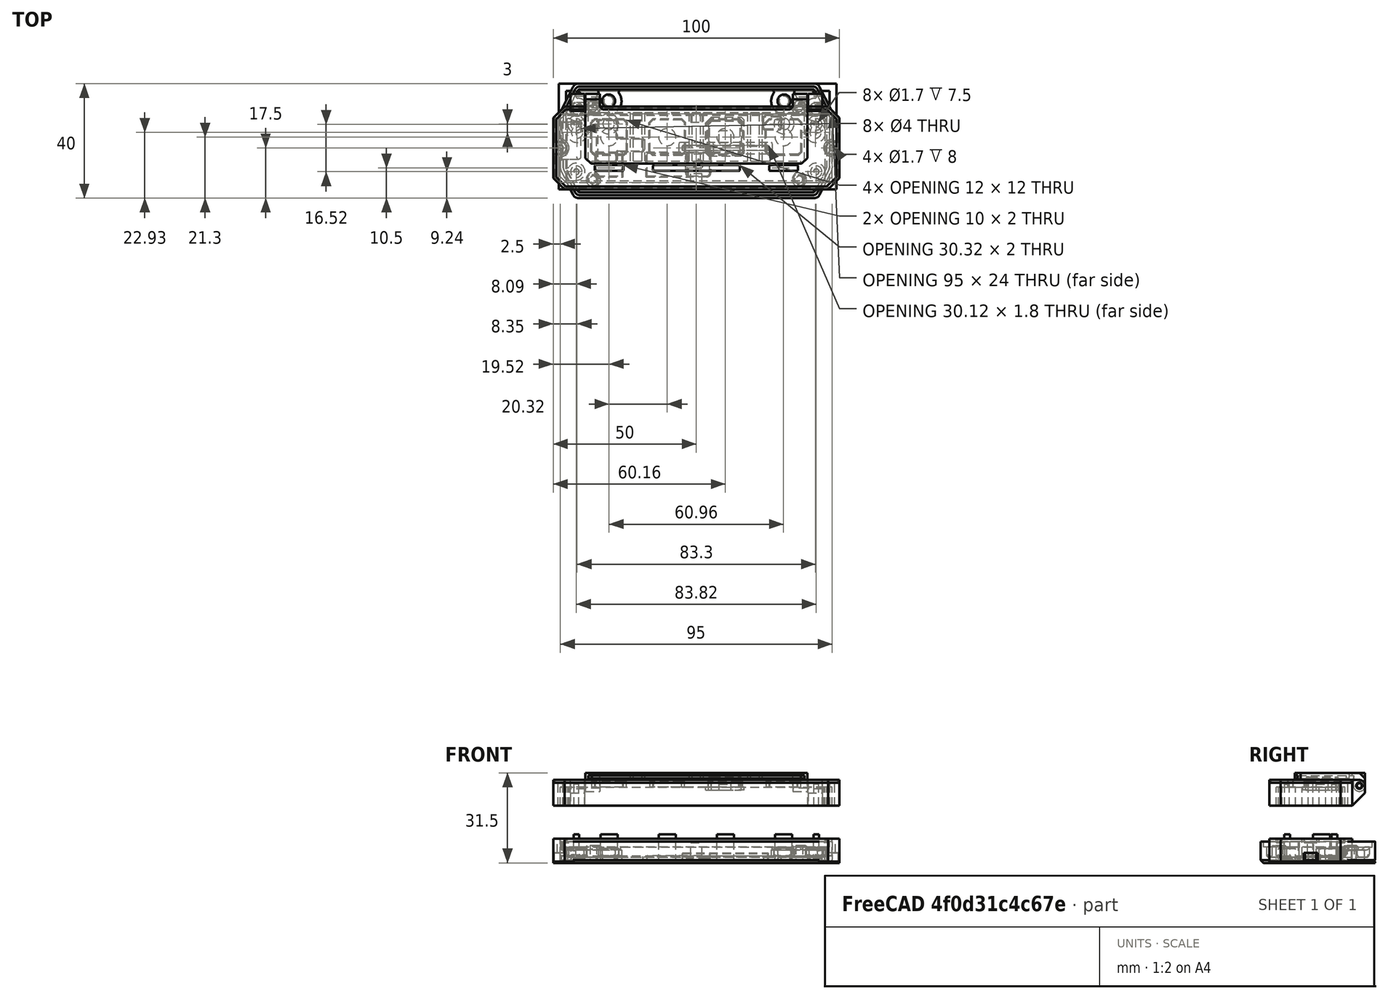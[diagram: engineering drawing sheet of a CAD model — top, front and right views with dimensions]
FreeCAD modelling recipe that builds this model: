
FCSTD DOCUMENT  (FreeCAD 0.18R16146 (Git))
Label: klipper-button
License: All rights reserved
LicenseURL: http://en.wikipedia.org/wiki/All_rights_reserved
objects: Part::Cylinder×46, Part::Box×43, Part::MultiFuse×27, Part::Cut×23, Part::Chamfer×19, Part::Feature×11, Part::Fillet×4
note: 173 computed .brp shape members not serialized (recipe doc carries the construction recipe); baked Part::Feature solids carry a one-line shape summary decoded from their .brp

FEATURE [Part::Feature] Part__Feature001001  label="Housing002"
  Placement = pos=(-10,2.5,0) rot=(0,0,1;0rad)
  shape: bbox 95.02 x 40.02 x 7.633 mm, 303 faces (baked)
FEATURE [Part::Cylinder] Cylinder
  Angle = 360
  AttacherType = Attacher::AttachEngine3D
  Height = 10
  Placement = pos=(-25.65,13.93,0) rot=(0,0,1;0rad)
  Radius = 2
FEATURE [Part::Cylinder] Cylinder001
  Angle = 360
  AttacherType = Attacher::AttachEngine3D
  Height = 10
  Placement = pos=(-36.65,10.93,0) rot=(0,0,1;0rad)
  Radius = 2
FEATURE [Part::Cylinder] Cylinder002
  Angle = 360
  AttacherType = Attacher::AttachEngine3D
  Height = 10
  Placement = pos=(46.65,10.93,0) rot=(0,0,1;0rad)
  Radius = 2
FEATURE [Part::Cylinder] Cylinder003
  Angle = 360
  AttacherType = Attacher::AttachEngine3D
  Height = 10
  Placement = pos=(35.65,13.93,0) rot=(0,0,1;0rad)
  Radius = 2
FEATURE [Part::Box] Box  label="PCB"
  AttacherType = Attacher::AttachEngine3D
  Height = 1
  Length = 90.17
  Placement = pos=(-45.085,-11.43,7.5) rot=(0,0,1;0rad)
  Width = 22.86
FEATURE [Part::Cylinder] Cylinder004
  Angle = 360
  AttacherType = Attacher::AttachEngine3D
  Height = 7.5
  Placement = pos=(-41.91,8.255,0) rot=(0,0,1;0rad)
  Radius = 0.85
FEATURE [Part::Cylinder] Cylinder005
  Angle = 360
  AttacherType = Attacher::AttachEngine3D
  Height = 7.5
  Placement = pos=(-41.91,-8.26,0) rot=(0,0,1;0rad)
  Radius = 0.85
FEATURE [Part::Cylinder] Cylinder006
  Angle = 360
  AttacherType = Attacher::AttachEngine3D
  Height = 7.5
  Placement = pos=(41.91,8.26,0) rot=(0,0,1;0rad)
  Radius = 0.85
FEATURE [Part::Cylinder] Cylinder007
  Angle = 360
  AttacherType = Attacher::AttachEngine3D
  Height = 7.5
  Placement = pos=(41.91,-8.26,0) rot=(0,0,1;0rad)
  Radius = 0.85
FEATURE [Part::Cylinder] Cylinder008
  Angle = 360
  AttacherType = Attacher::AttachEngine3D
  Height = 10
  Placement = pos=(-10.16,3.81,0) rot=(0,0,1;0rad)
  Radius = 3
FEATURE [Part::Cylinder] Cylinder009
  Angle = 360
  AttacherType = Attacher::AttachEngine3D
  Height = 10
  Placement = pos=(10.16,3.81,0) rot=(0,0,1;0rad)
  Radius = 3
FEATURE [Part::Cylinder] Cylinder010
  Angle = 360
  AttacherType = Attacher::AttachEngine3D
  Height = 10
  Placement = pos=(30.48,3.81,0) rot=(0,0,1;0rad)
  Radius = 3
FEATURE [Part::Cylinder] Cylinder011
  Angle = 360
  AttacherType = Attacher::AttachEngine3D
  Height = 10
  Placement = pos=(-30.48,3.81,0) rot=(0,0,1;0rad)
  Radius = 3
FEATURE [Part::MultiFuse] Fusion002  label="button"
  Shapes = -> [Cylinder011,Cylinder010,Cylinder009,Cylinder008]
FEATURE [Part::Box] Box001  label="Cube001"
  AttacherType = Attacher::AttachEngine3D
  Height = 0.5
  Length = 97
  Placement = pos=(-48,-14.5,0) rot=(0,0,1;0rad)
  Width = 37
FEATURE [Part::Box] Box002  label="Cube002"
  AttacherType = Attacher::AttachEngine3D
  Height = 0.5
  Length = 92
  Placement = pos=(-45.5,-12,0) rot=(0,0,1;0rad)
  Width = 32
FEATURE [Part::Box] Box003  label="Cube003"
  AttacherType = Attacher::AttachEngine3D
  Height = 22.5
  Length = 95
  Placement = pos=(-47.5,-12,2.5) rot=(0,0,1;0rad)
  Width = 24
FEATURE [Part::Box] Box004  label="Cube004"
  AttacherType = Attacher::AttachEngine3D
  Height = 8.5
  Length = 100
  Placement = pos=(-50,-14.5,0) rot=(0,0,1;0rad)
  Width = 29
FEATURE [Part::Cylinder] Cylinder012
  Angle = 360
  AttacherType = Attacher::AttachEngine3D
  Height = 5
  Placement = pos=(46.65,10.93,0) rot=(0,0,1;0rad)
  Radius = 3.5
FEATURE [Part::Cylinder] Cylinder013
  Angle = 360
  AttacherType = Attacher::AttachEngine3D
  Height = 5
  Placement = pos=(-25.65,13.93,0) rot=(0,0,1;0rad)
  Radius = 3.5
FEATURE [Part::Cylinder] Cylinder014
  Angle = 360
  AttacherType = Attacher::AttachEngine3D
  Height = 5
  Placement = pos=(-36.65,10.93,0) rot=(0,0,1;0rad)
  Radius = 3.5
FEATURE [Part::Cylinder] Cylinder015
  Angle = 360
  AttacherType = Attacher::AttachEngine3D
  Height = 5
  Placement = pos=(35.65,13.93,0) rot=(0,0,1;0rad)
  Radius = 3.5
FEATURE [Part::MultiFuse] Fusion
  Placement = pos=(-5,-5.5,0) rot=(0,0,1;0rad)
  Shapes = -> [Cylinder002,Cylinder,Cylinder001,Cylinder003]
FEATURE [Part::MultiFuse] Fusion003
  Placement = pos=(-5,-5.5,0) rot=(0,0,1;0rad)
  Shapes = -> [Cylinder015,Cylinder014,Cylinder013,Cylinder012]
FEATURE [Part::Cylinder] Cylinder016
  Angle = 360
  AttacherType = Attacher::AttachEngine3D
  Height = 5
  Placement = pos=(-41.91,8.255,0) rot=(0,0,1;0rad)
  Radius = 3
FEATURE [Part::Cylinder] Cylinder017
  Angle = 360
  AttacherType = Attacher::AttachEngine3D
  Height = 5
  Placement = pos=(-41.91,-8.26,0) rot=(0,0,1;0rad)
  Radius = 3
FEATURE [Part::Cylinder] Cylinder018
  Angle = 360
  AttacherType = Attacher::AttachEngine3D
  Height = 5
  Placement = pos=(41.91,8.26,0) rot=(0,0,1;0rad)
  Radius = 3
FEATURE [Part::Cylinder] Cylinder019
  Angle = 360
  AttacherType = Attacher::AttachEngine3D
  Height = 5
  Placement = pos=(41.91,-8.26,0) rot=(0,0,1;0rad)
  Radius = 3
FEATURE [Part::MultiFuse] Fusion006
  Shapes = -> [Cylinder019,Cylinder016,Cylinder017,Cylinder018]
FEATURE [Part::Cylinder] Cylinder020
  Angle = 360
  AttacherType = Attacher::AttachEngine3D
  Height = 10
  Placement = pos=(41.91,-8.26,0) rot=(0,0,1;0rad)
  Radius = 1
FEATURE [Part::Cylinder] Cylinder021
  Angle = 360
  AttacherType = Attacher::AttachEngine3D
  Height = 10
  Placement = pos=(41.91,8.26,0) rot=(0,0,1;0rad)
  Radius = 1
FEATURE [Part::Cylinder] Cylinder022
  Angle = 360
  AttacherType = Attacher::AttachEngine3D
  Height = 10
  Placement = pos=(-41.91,-8.26,0) rot=(0,0,1;0rad)
  Radius = 1
FEATURE [Part::Cylinder] Cylinder023
  Angle = 360
  AttacherType = Attacher::AttachEngine3D
  Height = 10
  Placement = pos=(-41.91,8.255,0) rot=(0,0,1;0rad)
  Radius = 1
FEATURE [Part::MultiFuse] Fusion008
  Shapes = -> [Cylinder020,Cylinder021,Cylinder023,Cylinder022]
FEATURE [Part::Box] Box005  label="Cube"
  AttacherType = Attacher::AttachEngine3D
  Height = 10
  Length = 9
  Placement = pos=(-34.974,-10.755,0) rot=(0,0,1;0rad)
  Width = 8
FEATURE [Part::Box] Box006  label="Cube005"
  AttacherType = Attacher::AttachEngine3D
  Height = 10
  Length = 14
  Placement = pos=(-17.154,-10.755,0) rot=(0,0,1;0rad)
  Width = 8
FEATURE [Part::Cylinder] Cylinder024
  Angle = 360
  AttacherType = Attacher::AttachEngine3D
  Height = 1.5
  Placement = pos=(41.91,-8.26,0) rot=(0,0,1;0rad)
  Radius = 2
FEATURE [Part::Cylinder] Cylinder025
  Angle = 360
  AttacherType = Attacher::AttachEngine3D
  Height = 1.5
  Placement = pos=(-41.91,8.255,0) rot=(0,0,1;0rad)
  Radius = 2
FEATURE [Part::Cylinder] Cylinder026
  Angle = 360
  AttacherType = Attacher::AttachEngine3D
  Height = 1.5
  Placement = pos=(-41.91,-8.26,0) rot=(0,0,1;0rad)
  Radius = 2
FEATURE [Part::Cylinder] Cylinder027
  Angle = 360
  AttacherType = Attacher::AttachEngine3D
  Height = 1.5
  Placement = pos=(41.91,8.26,0) rot=(0,0,1;0rad)
  Radius = 2
FEATURE [Part::MultiFuse] Fusion012
  Shapes = -> [Cylinder027,Cylinder026,Cylinder025,Cylinder024]
FEATURE [Part::Box] Box008  label="Cube007"
  AttacherType = Attacher::AttachEngine3D
  Height = 6.5
  Length = 95
  Placement = pos=(-47.5,-12,20) rot=(0,0,1;0rad)
  Width = 24
FEATURE [Part::Cylinder] Cylinder028
  Angle = 360
  AttacherType = Attacher::AttachEngine3D
  Height = 8
  Placement = pos=(41.91,-8.26,0) rot=(0,0,1;0rad)
  Radius = 3
FEATURE [Part::Cylinder] Cylinder029
  Angle = 360
  AttacherType = Attacher::AttachEngine3D
  Height = 8
  Placement = pos=(-41.91,8.255,0) rot=(0,0,1;0rad)
  Radius = 3
FEATURE [Part::Cylinder] Cylinder030
  Angle = 360
  AttacherType = Attacher::AttachEngine3D
  Height = 8
  Placement = pos=(41.91,8.26,0) rot=(0,0,1;0rad)
  Radius = 3
FEATURE [Part::Cylinder] Cylinder031
  Angle = 360
  AttacherType = Attacher::AttachEngine3D
  Height = 8
  Placement = pos=(-41.91,-8.26,0) rot=(0,0,1;0rad)
  Radius = 3
FEATURE [Part::MultiFuse] Fusion013
  Placement = pos=(0,0,20) rot=(0,0,1;0rad)
  Shapes = -> [Cylinder031,Cylinder030,Cylinder029,Cylinder028]
FEATURE [Part::MultiFuse] Fusion015
  Placement = pos=(0,0,20) rot=(0,0,1;0rad)
  Shapes = -> [Cylinder006,Cylinder005,Cylinder004,Cylinder007]
FEATURE [Part::Box] Box009  label="Cube008"
  AttacherType = Attacher::AttachEngine3D
  Height = 10
  Length = 12
  Placement = pos=(-16.16,-6,0) rot=(0,0,1;0rad)
  Width = 12
FEATURE [Part::Box] Box010  label="Cube009"
  AttacherType = Attacher::AttachEngine3D
  Height = 10
  Length = 12
  Placement = pos=(4.16,-6,0) rot=(0,0,1;0rad)
  Width = 12
FEATURE [Part::Box] Box011  label="Cube010"
  AttacherType = Attacher::AttachEngine3D
  Height = 10
  Length = 12
  Placement = pos=(24.48,-6,0) rot=(0,0,1;0rad)
  Width = 12
FEATURE [Part::Box] Box012  label="Cube011"
  AttacherType = Attacher::AttachEngine3D
  Height = 10
  Length = 12
  Placement = pos=(-36.48,-6,0) rot=(0,0,1;0rad)
  Width = 12
FEATURE [Part::MultiFuse] Fusion016
  Placement = pos=(0,0,25) rot=(0,0,1;0rad)
  Shapes = -> [Box012,Box011,Box010,Box009]
FEATURE [Part::Chamfer] Chamfer007
  Base = -> Fusion016
  Edges = 16 edges r=1: [Edge1,Edge3,Edge5,Edge7,Edge13,Edge15,Edge17,Edge19,Edge25,Edge27,Edge29,Edge31,Edge37,Edge39,Edge41,Edge43]
  Placement = pos=(0,3.8,0) rot=(0,0,1;0rad)
FEATURE [Part::Cut] Cut
  Base = -> Box004
  Tool = -> Box003
FEATURE [Part::MultiFuse] Fusion017
  Shapes = -> [Cut,Fusion003]
FEATURE [Part::Cut] Cut008
  Base = -> Fusion017
  Tool = -> Fusion
FEATURE [Part::Box] Box007  label="Cube006"
  AttacherType = Attacher::AttachEngine3D
  Height = 9
  Length = 100
  Placement = pos=(-50,-14.5,20) rot=(0,0,1;0rad)
  Width = 29
FEATURE [Part::Cut] Cut010
  Base = -> Box007
  Tool = -> Box008
FEATURE [Part::MultiFuse] Fusion018
  Shapes = -> [Fusion013,Cut010]
FEATURE [Part::Cut] Cut011
  Base = -> Fusion018
  Tool = -> Fusion015
FEATURE [Part::Cylinder] Cylinder032
  Angle = 360
  AttacherType = Attacher::AttachEngine3D
  Height = 8
  Placement = pos=(-47.5,0,20) rot=(0,0,1;0rad)
  Radius = 3
FEATURE [Part::Cylinder] Cylinder033
  Angle = 360
  AttacherType = Attacher::AttachEngine3D
  Height = 8
  Placement = pos=(47.5,0,20) rot=(0,0,1;0rad)
  Radius = 3
FEATURE [Part::Cylinder] Cylinder034
  Angle = 360
  AttacherType = Attacher::AttachEngine3D
  Height = 3.5
  Placement = pos=(47.5,0,0) rot=(0,0,1;0rad)
  Radius = 2
FEATURE [Part::Cylinder] Cylinder035
  Angle = 360
  AttacherType = Attacher::AttachEngine3D
  Height = 3.5
  Placement = pos=(-47.5,0,0) rot=(0,0,1;0rad)
  Radius = 2
FEATURE [Part::Cylinder] Cylinder036
  Angle = 360
  AttacherType = Attacher::AttachEngine3D
  Height = 8.5
  Placement = pos=(-47.5,0,0) rot=(0,0,1;0rad)
  Radius = 3
FEATURE [Part::Cylinder] Cylinder037
  Angle = 360
  AttacherType = Attacher::AttachEngine3D
  Height = 8.5
  Placement = pos=(47.5,0,0) rot=(0,0,1;0rad)
  Radius = 3
FEATURE [Part::Box] Box013  label="Cube012"
  AttacherType = Attacher::AttachEngine3D
  Height = 10
  Length = 10
  Placement = pos=(50,-4.5,0) rot=(0,0,1;0rad)
  Width = 10
FEATURE [Part::Box] Box014  label="Cube013"
  AttacherType = Attacher::AttachEngine3D
  Height = 10
  Length = 10
  Placement = pos=(-60,-4.5,0) rot=(0,0,1;0rad)
  Width = 10
FEATURE [Part::Cut] Cut013
  Base = -> Cylinder036
  Tool = -> Box014
FEATURE [Part::Cut] Cut014
  Base = -> Cylinder037
  Tool = -> Box013
FEATURE [Part::Box] Box015  label="Cube014"
  AttacherType = Attacher::AttachEngine3D
  Height = 10
  Length = 10
  Placement = pos=(35.5,-3.5,7) rot=(0,0,1;0rad)
  Width = 10
FEATURE [Part::Box] Box016  label="Cube015"
  AttacherType = Attacher::AttachEngine3D
  Height = 10
  Length = 10
  Placement = pos=(-45.5,-3.5,7) rot=(0,0,1;0rad)
  Width = 10
FEATURE [Part::Cut] Cut015
  Base = -> Cut013
  Tool = -> Box016
FEATURE [Part::Cut] Cut016
  Base = -> Cut014
  Tool = -> Box015
FEATURE [Part::Cylinder] Cylinder038
  Angle = 360
  AttacherType = Attacher::AttachEngine3D
  Height = 8.5
  Placement = pos=(-47.5,0,0) rot=(0,0,1;0rad)
  Radius = 1.1
FEATURE [Part::Cylinder] Cylinder039
  Angle = 360
  AttacherType = Attacher::AttachEngine3D
  Height = 8.5
  Placement = pos=(47.5,0,0) rot=(0,0,1;0rad)
  Radius = 1.1
FEATURE [Part::Box] Box017  label="Cube016"
  AttacherType = Attacher::AttachEngine3D
  Height = 3.5
  Length = 7
  Placement = pos=(-54.5,-2,0) rot=(0,0,1;0rad)
  Width = 4
FEATURE [Part::Box] Box018  label="Cube017"
  AttacherType = Attacher::AttachEngine3D
  Height = 3.5
  Length = 7
  Placement = pos=(47.5,-2,0) rot=(0,0,1;0rad)
  Width = 4
FEATURE [Part::MultiFuse] Fusion021
  Shapes = -> [Box018,Box017,Cylinder035,Cylinder034]
FEATURE [Part::Cut] Cut019
  Base = -> Cut011
  Tool = -> Chamfer007
FEATURE [Part::Cylinder] Cylinder040
  Angle = 360
  AttacherType = Attacher::AttachEngine3D
  Height = 8
  Placement = pos=(47.5,0,20) rot=(0,0,1;0rad)
  Radius = 0.85
FEATURE [Part::Cylinder] Cylinder041
  Angle = 360
  AttacherType = Attacher::AttachEngine3D
  Height = 8
  Placement = pos=(-47.5,0,20) rot=(0,0,1;0rad)
  Radius = 0.85
FEATURE [Part::Box] Box019  label="Cube018"
  AttacherType = Attacher::AttachEngine3D
  Height = 10
  Length = 10
  Placement = pos=(50,-3,20) rot=(0,0,1;0rad)
  Width = 10
FEATURE [Part::Box] Box020  label="Cube019"
  AttacherType = Attacher::AttachEngine3D
  Height = 10
  Length = 10
  Placement = pos=(-60,-3,20) rot=(0,0,1;0rad)
  Width = 10
FEATURE [Part::Cut] Cut020
  Base = -> Cylinder032
  Tool = -> Box020
FEATURE [Part::Cut] Cut021
  Base = -> Cylinder033
  Tool = -> Box019
FEATURE [Part::MultiFuse] Fusion022
  Shapes = -> [Cut021,Cut020]
FEATURE [Part::MultiFuse] Fusion023
  Shapes = -> [Cut019,Fusion022]
FEATURE [Part::MultiFuse] Fusion024
  Shapes = -> [Cylinder040,Cylinder041]
FEATURE [Part::Cut] Cut022
  Base = -> Fusion023
  Tool = -> Fusion024
FEATURE [Part::MultiFuse] Fusion025
  Shapes = -> [Cylinder038,Cylinder039]
FEATURE [Part::MultiFuse] Fusion026
  Shapes = -> [Cut016,Cut015]
FEATURE [Part::Chamfer] Chamfer010
  Base = -> Cut022
  Edges = 4 edges r=2: [Edge51,Edge56,Edge59,Edge65]
FEATURE [Part::Chamfer] Chamfer011
  Base = -> Chamfer010
  Edges = 4 edges r=4: [Edge175,Edge179,Edge180,Edge181]
FEATURE [Part::Feature] Chamfer011001  label="Chamfer012"
  shape: bbox 100 x 29 x 9 mm, 75 faces (baked)
FEATURE [Part::Chamfer] Chamfer011003
  Base = -> Chamfer011001
  Edges = 32 edges r=0.4: [Edge64,Edge81,Edge82,Edge83,Edge84,Edge85,Edge86,Edge87,Edge88,Edge89,Edge90,Edge91,Edge92,Edge93,Edge94,Edge95,Edge96,Edge97,Edge98,Edge99,Edge100,Edge101,Edge102,Edge103,Edge104,Edge105,Edge106,Edge107,Edge108,Edge109,Edge110,Edge111]
FEATURE [Part::Chamfer] Chamfer011004
  Base = -> Chamfer011003
  Edges = 8 edges r=1: [Edge70,Edge71,Edge72,Edge73,Edge74,Edge75,Edge76,Edge77]
FEATURE [Part::MultiFuse] Fusion011002
  Placement = pos=(0,1,0) rot=(0,0,1;0rad)
  Shapes = -> [Box005,Box006]
FEATURE [Part::MultiFuse] Fusion011003
  Shapes = -> [Fusion026,Cut008]
FEATURE [Part::Cut] Cut023
  Base = -> Fusion011003
  Tool = -> Fusion025
FEATURE [Part::Cut] Cut024
  Base = -> Cut023
  Tool = -> Fusion021
FEATURE [Part::Chamfer] Chamfer
  Base = -> Cut024
  Edges = 4 edges r=2: [Edge55,Edge57,Edge76,Edge79]
FEATURE [Part::Chamfer] Chamfer011005
  Base = -> Chamfer
  Edges = 4 edges r=4: [Edge24,Edge32,Edge139,Edge141]
FEATURE [Part::Cut] Cut025
  Base = -> Chamfer011005
  Tool = -> Fusion011002
FEATURE [Part::Feature] Cut025001  label="Cut026"
  shape: bbox 100 x 29 x 8.5 mm, 57 faces (baked)
FEATURE [Part::Chamfer] Chamfer011006
  Base = -> Cut025001
  Edges = 29 edges r=0.4: [Edge1,Edge5,Edge8,Edge38,Edge41,Edge43,Edge82,Edge84,Edge86,Edge87,Edge90,Edge92,Edge94,Edge95,Edge135,Edge136,Edge138,Edge139,Edge140,Edge144,Edge146,Edge148,Edge149,Edge151,Edge152,Edge153,Edge156,Edge159,Edge160]
FEATURE [Part::Box] Box021  label="Cube020"
  AttacherType = Attacher::AttachEngine3D
  Height = 7
  Length = 4
  Placement = pos=(-2,9,0) rot=(0,0,1;0rad)
  Width = 3
FEATURE [Part::Box] Box022  label="Cube021"
  AttacherType = Attacher::AttachEngine3D
  Height = 7
  Length = 4
  Placement = pos=(-2,-12,0) rot=(0,0,1;0rad)
  Width = 3
FEATURE [Part::MultiFuse] Fusion011004  label="bottom"
  Shapes = -> [Box021,Chamfer011006,Box022]
FEATURE [Part::Box] Box023  label="Cube022"
  AttacherType = Attacher::AttachEngine3D
  Height = 4.5
  Length = 11.5
  Placement = pos=(-5.75,-5.75,0) rot=(0,0,1;0rad)
  Width = 11.5
FEATURE [Part::Box] Box024  label="Cube023"
  AttacherType = Attacher::AttachEngine3D
  Height = 1
  Length = 13.5
  Placement = pos=(-6.75,-6.75,0) rot=(0,0,1;0rad)
  Width = 13.5
FEATURE [Part::Chamfer] Chamfer011008
  Base = -> Box024
  Edges = 3 edges r=1: [Edge1,Edge5,Edge7]
FEATURE [Part::Chamfer] Chamfer011009
  Base = -> Chamfer011008
  Edges = 1 edges r=2: [Edge3]
FEATURE [Part::Box] Box025  label="Cube024"
  AttacherType = Attacher::AttachEngine3D
  Height = 2
  Length = 4.2
  Placement = pos=(-2.1,-2.1,0) rot=(0,0,1;0rad)
  Width = 4.2
FEATURE [Part::Chamfer] Chamfer011010
  Base = -> Box023
  Edges = 4 edges r=1: [Edge1,Edge3,Edge5,Edge7]
FEATURE [Part::Chamfer] Chamfer011011
  Base = -> Chamfer011010
  Edges = 8 edges r=0.4: [Edge1,Edge5,Edge6,Edge7,Edge8,Edge9,Edge10,Edge11]
FEATURE [Part::MultiFuse] Fusion011005
  Shapes = -> [Chamfer011011,Chamfer011009]
FEATURE [Part::Cut] Cut025002002  label="button001"
  Base = -> Fusion011005
  Placement = pos=(10,4,25.5) rot=(0,0,1;0rad)
  Tool = -> Box025
FEATURE [Part::Box] Box026  label="Cube025"
  AttacherType = Attacher::AttachEngine3D
  Height = 9
  Length = 5
  Placement = pos=(-44,13,20) rot=(0,0,1;0rad)
  Width = 6
FEATURE [Part::Box] Box027  label="Cube026"
  AttacherType = Attacher::AttachEngine3D
  Height = 9
  Length = 5
  Placement = pos=(39,13,20) rot=(0,0,1;0rad)
  Width = 6
FEATURE [Part::Cylinder] Cylinder042
  Angle = 360
  AttacherType = Attacher::AttachEngine3D
  Height = 10
  Placement = pos=(-37,17,27) rot=(0,-1,0;1.5708rad)
  Radius = 1.1
FEATURE [Part::Cylinder] Cylinder043
  Angle = 360
  AttacherType = Attacher::AttachEngine3D
  Height = 10
  Placement = pos=(47,17,27) rot=(0,-1,0;1.5708rad)
  Radius = 1.1
FEATURE [Part::Box] Box028  label="Cube027"
  AttacherType = Attacher::AttachEngine3D
  Height = 2.5
  Length = 77.5
  Placement = pos=(-38.75,-5.5,29) rot=(0,0,1;0rad)
  Width = 24.5
FEATURE [Part::Box] Box029  label="Cube028"
  AttacherType = Attacher::AttachEngine3D
  Height = 1.5
  Length = 75.5
  Placement = pos=(-37.75,-5.5,29) rot=(0,0,1;0rad)
  Width = 24.5
FEATURE [Part::Box] Box030  label="Cube029"
  AttacherType = Attacher::AttachEngine3D
  Height = 6.5
  Length = 5
  Placement = pos=(-38.75,15,25) rot=(0,0,1;0rad)
  Width = 4
FEATURE [Part::Box] Box031  label="Cube030"
  AttacherType = Attacher::AttachEngine3D
  Height = 6.5
  Length = 5
  Placement = pos=(33.75,15,25) rot=(0,0,1;0rad)
  Width = 4
FEATURE [Part::Fillet] Fillet002
  Base = -> Box031
  Edges = 2 edges r=1.99: [Edge9,Edge11]
FEATURE [Part::Fillet] Fillet003
  Base = -> Box030
  Edges = 2 edges r=1.99: [Edge9,Edge11]
FEATURE [Part::Cylinder] Cylinder044
  Angle = 360
  AttacherType = Attacher::AttachEngine3D
  Height = 10
  Placement = pos=(41.5,17,27) rot=(0,-1,0;1.5708rad)
  Radius = 0.85
FEATURE [Part::Cylinder] Cylinder045
  Angle = 360
  AttacherType = Attacher::AttachEngine3D
  Height = 10
  Placement = pos=(-32.5,17,27) rot=(0,-1,0;1.5708rad)
  Radius = 0.85
FEATURE [Part::Cut] Cut025002006
  Base = -> Fillet003
  Tool = -> Cylinder045
FEATURE [Part::Cut] Cut025002007
  Base = -> Fillet002
  Tool = -> Cylinder044
FEATURE [Part::Box] Box032  label="Cube031"
  AttacherType = Attacher::AttachEngine3D
  Height = 4.5
  Length = 67.5
  Placement = pos=(-33.75,13.5,29) rot=(0,0,1;0rad)
  Width = 20
FEATURE [Part::MultiFuse] Fusion011007
  Shapes = -> [Cut025002006,Cut025002007]
FEATURE [Part::Chamfer] Chamfer011012
  Base = -> Box028
  Edges = 2 edges r=2: [Edge1,Edge5]
FEATURE [Part::Cut] Cut025002008
  Base = -> Chamfer011012
  Tool = -> Box029
FEATURE [Part::MultiFuse] Fusion011008
  Shapes = -> [Fusion011007,Cut025002008]
FEATURE [Part::Chamfer] Chamfer011013
  Base = -> Box032
  Edges = 2 edges r=1: [Edge1,Edge5]
FEATURE [Part::Cut] Cut025002009
  Base = -> Fusion011008
  Tool = -> Chamfer011013
FEATURE [Part::Feature] Cut025002009001  label="Cut025002010"
  shape: bbox 77.5 x 24.5 x 6.5 mm, 28 faces (baked)
FEATURE [Part::Chamfer] Chamfer011014
  Base = -> Cut025002009001
  Edges = 2 edges r=2: [Edge68,Edge72]
FEATURE [Part::Feature] Chamfer011015001  label="Chamfer011016"
  shape: bbox 10 x 2 x 10 mm, 10 faces (baked)
FEATURE [Part::Feature] Chamfer011015002  label="Chamfer011017"
  Placement = pos=(20.32,0,0) rot=(0,0,1;0rad)
  shape: bbox 10 x 2 x 10 mm, 10 faces (baked)
FEATURE [Part::Feature] Chamfer011015003  label="Chamfer011018"
  Placement = pos=(40.64,0,0) rot=(0,0,1;0rad)
  shape: bbox 10 x 2 x 10 mm, 10 faces (baked)
FEATURE [Part::Feature] Chamfer011015004  label="Chamfer011019"
  Placement = pos=(60.96,0,0) rot=(0,0,1;0rad)
  shape: bbox 10 x 2 x 10 mm, 10 faces (baked)
FEATURE [Part::Fillet] Fillet
  Base = -> Box026
  Edges = 1 edges r=2: [Edge12]
FEATURE [Part::Fillet] Fillet004
  Base = -> Box027
  Edges = 1 edges r=2: [Edge12]
FEATURE [Part::Chamfer] Chamfer011015005
  Base = -> Fillet
  Edges = 1 edges r=4.5: [Edge14]
FEATURE [Part::Chamfer] Chamfer011015006
  Base = -> Fillet004
  Edges = 1 edges r=4.5: [Edge14]
FEATURE [Part::Cut] Cut025002009002
  Base = -> Chamfer011015005
  Tool = -> Cylinder042
FEATURE [Part::Cut] Cut025002009003
  Base = -> Chamfer011015006
  Tool = -> Cylinder043
FEATURE [Part::MultiFuse] Fusion011010
  Shapes = -> [Cut025002009002,Cut025002009003]
FEATURE [Part::Box] Box033  label="Cube032"
  AttacherType = Attacher::AttachEngine3D
  Height = 3.5
  Length = 30.12
  Placement = pos=(-4.9,-0.9,0) rot=(0,0,1;0rad)
  Width = 1.8
FEATURE [Part::Box] Box034  label="Cube033"
  AttacherType = Attacher::AttachEngine3D
  Height = 1
  Length = 32.6
  Placement = pos=(-6,-2,0) rot=(0,0,1;0rad)
  Width = 4
FEATURE [Part::Box] Box035  label="Cube034"
  AttacherType = Attacher::AttachEngine3D
  Height = 1
  Length = 76
  Placement = pos=(-38,12.5,29.5) rot=(0,0,1;0rad)
  Width = 1
FEATURE [Part::Box] Box036  label="Cube035"
  AttacherType = Attacher::AttachEngine3D
  Height = 1
  Length = 73
  Placement = pos=(-36.5,-5.5,29.5) rot=(0,0,1;0rad)
  Width = 1
FEATURE [Part::Box] Box037  label="Cube036"
  AttacherType = Attacher::AttachEngine3D
  Height = 1
  Length = 1
  Placement = pos=(22,-5.5,29.5) rot=(0,0,1;0rad)
  Width = 18
FEATURE [Part::Box] Box038  label="Cube037"
  AttacherType = Attacher::AttachEngine3D
  Height = 1
  Length = 1
  Placement = pos=(-23,-5.5,29.5) rot=(0,0,1;0rad)
  Width = 18
FEATURE [Part::Box] Box039  label="Cube038"
  AttacherType = Attacher::AttachEngine3D
  Height = 1
  Length = 1
  Placement = pos=(-2.5,-5.5,29.5) rot=(0,0,1;0rad)
  Width = 18
FEATURE [Part::Box] Box040  label="Cube039"
  AttacherType = Attacher::AttachEngine3D
  Height = 1
  Length = 1
  Placement = pos=(1.5,-5.5,29.5) rot=(0,0,1;0rad)
  Width = 18
FEATURE [Part::Box] Box041  label="Cube040"
  AttacherType = Attacher::AttachEngine3D
  Height = 1
  Length = 1
  Placement = pos=(-19,-5.5,29.5) rot=(0,0,1;0rad)
  Width = 18
FEATURE [Part::Box] Box042  label="Cube041"
  AttacherType = Attacher::AttachEngine3D
  Height = 1
  Length = 1
  Placement = pos=(18,-5.5,29.5) rot=(0,0,1;0rad)
  Width = 18
FEATURE [Part::MultiFuse] Fusion011013
  Shapes = -> [Box042,Box041,Box040,Box039,Box038,Box037,Chamfer011014,Box035,Box036]
FEATURE [Part::Feature] Chamfer011015009
  Placement = pos=(29.32,0,0) rot=(0,0,1;0rad)
  shape: bbox 10 x 2 x 10 mm, 10 faces (baked)
FEATURE [Part::Feature] Chamfer011015010
  Placement = pos=(32.82,0,0) rot=(0,0,1;0rad)
  shape: bbox 10 x 2 x 10 mm, 10 faces (baked)
FEATURE [Part::MultiFuse] Fusion011014
  Shapes = -> [Chamfer011015010,Chamfer011015009,Chamfer011015001,Chamfer011015002,Chamfer011015003,Chamfer011015004]
FEATURE [Part::Cut] Cut025002009004
  Base = -> Chamfer011004
  Tool = -> Fusion011014
FEATURE [Part::Feature] Fusion011012001  label="color-slot-short"
  shape: bbox 12 x 4 x 3.5 mm, 28 faces (baked)
FEATURE [Part::Chamfer] Chamfer011015011
  Base = -> Box033
  Edges = 8 edges r=0.2: [Edge1,Edge2,Edge3,Edge5,Edge6,Edge7,Edge10,Edge12]
FEATURE [Part::Chamfer] Chamfer011015012
  Base = -> Box034
  Edges = 4 edges r=0.4: [Edge1,Edge3,Edge5,Edge7]
FEATURE [Part::MultiFuse] Fusion011012002  label="color-slot-long"
  Shapes = -> [Chamfer011015012,Chamfer011015011]
